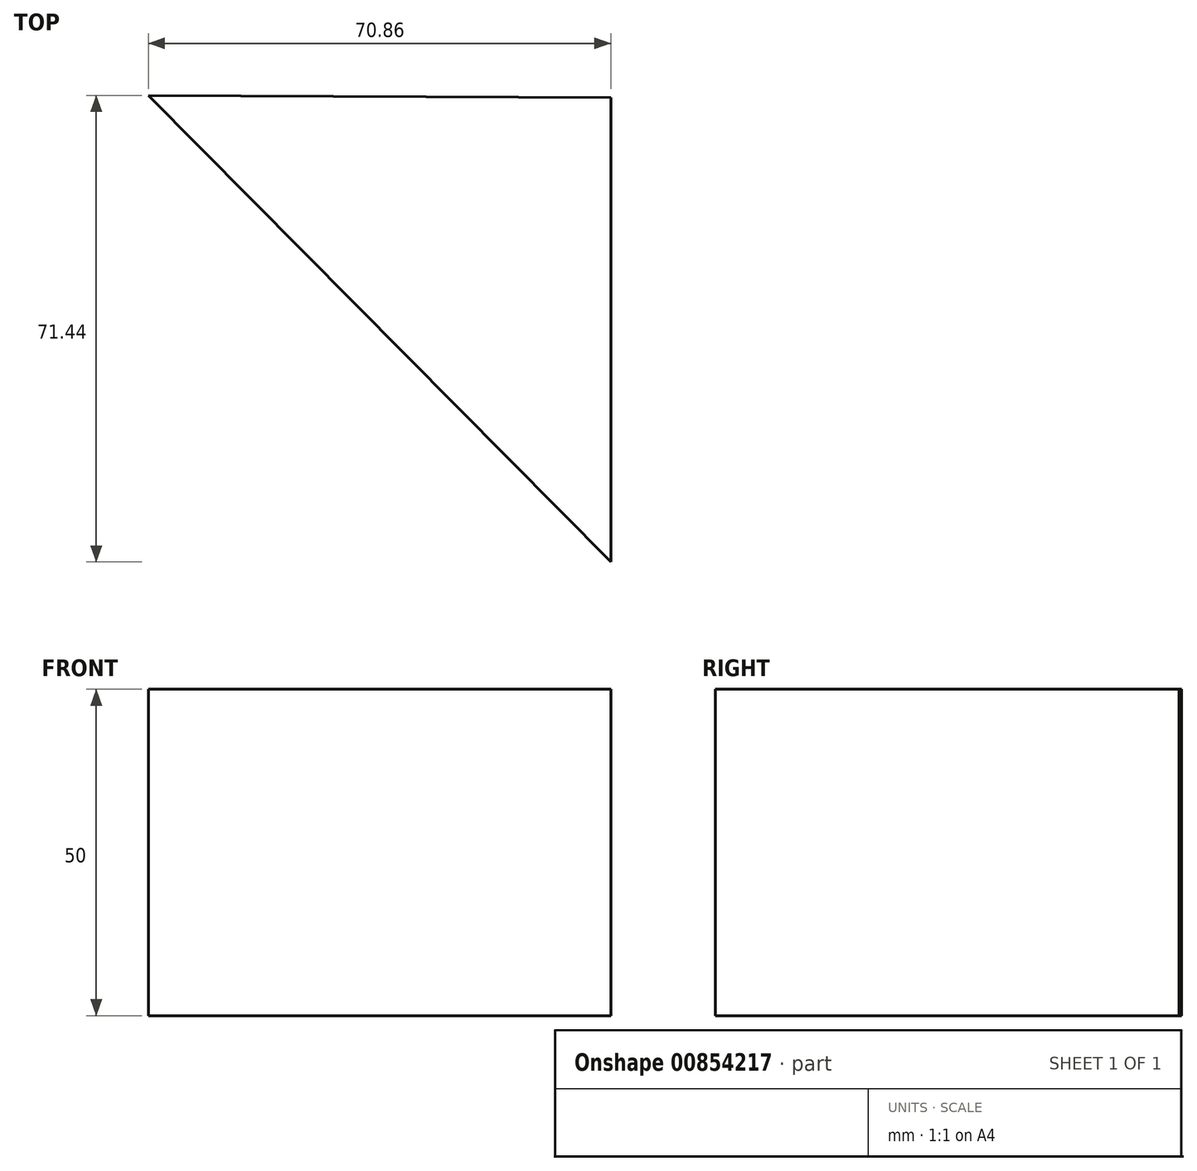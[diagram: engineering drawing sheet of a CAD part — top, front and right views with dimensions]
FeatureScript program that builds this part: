
annotation { "Feature Type Name" : "Feature", "Feature Type Description" : "" }
export const myFeature = defineFeature(function(context is Context, id is Id, definition is map)
    precondition{}
    {
        {
            var Q0;
            Q0=qCreatedBy(makeId("Top.planeOp"),FACE);
            var sketch = newSketch(context, id + "F0", { "sketchPlane" : qUnion([Q0])});
            skLineSegment(sketch, "E0", {"start": v(0, 0) * mm, "end": v(-70.86, 71.44) * mm});
            skLineSegment(sketch, "E1", {"start": v(-70.86, 71.44) * mm, "end": v(0, 71.1) * mm});
            skLineSegment(sketch, "E2", {"start": v(0, 71.1) * mm, "end": v(0, 0) * mm});
            skSolve(sketch);
        }
        {
            var Q0;
            Q0=makeQuery(id+"F0.imprint","IMPRINT",FACE,{"disambiguationData":[TD([[makeQuery(id+"F0.imprint","IMPRINT",EDGE,{"derivedFrom":sQuery(id+"F0.wireOp",EDGE,"E0")}),-1.0]])]});
            extrude(context, id + "F1", {"entities" : qUnion([Q0]), "depth" : 25 * mm, "offsetDistance" : 25 * mm});
        }
        {
            var Q0;
            Q0=makeQuery(id+"F1.opExtrude","CAP_FACE",FACE,{"disambiguationData":[OSD([sQuery(id+"F0.wireOp",EDGE,"E0"),sQuery(id+"F0.wireOp",EDGE,"E1"),sQuery(id+"F0.wireOp",EDGE,"E2")])],"isStart":false});
            extrude(context, id + "F2", {"entities" : qUnion([Q0]), "operationType" : NewBodyOperationType.ADD, "depth" : 25 * mm, "offsetDistance" : 25 * mm});
        }
    });
